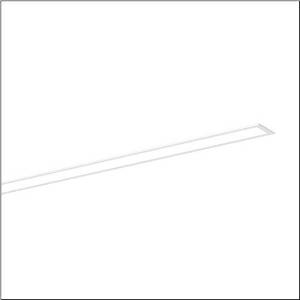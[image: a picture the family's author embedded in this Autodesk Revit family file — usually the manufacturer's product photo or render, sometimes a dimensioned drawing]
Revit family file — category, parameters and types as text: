
# Revit family: silica_r__21_51mx10db32wb_8ee9
name_source: partatom
category: Lighting Fixtures
units: mm (PartAtom-declared; Revit-internal decimal feet)

## family parameters
Cut with Voids When Loaded = No
Host = Face
Light Source = No
Part Type = Normal
Room Calculation Point = No
Round Connector Dimension = Use Diameter
Shared = No

## types (1)
- --- (1 x LED, 3000 lm, 20.2 W, 3000K)
    Apparent Load = 20 VA
    CIE Flux Codes = 48 79 96 100 100
    Color Rendering = 80
    Color Temperature = 3000K
    Default Elevation = 1800 mm
    Description = Silica® 21, office luminaire, primary optical cover: cover, of PMMA, opal, light emission: direct distribution, primary light characteristic: symmetric, installation type: recessed, LED, rated luminous flux: 3.000lm, luminous efficacy: 149lm/W, light colour: 830, colour temperature: 3000K, control gear: DALI 2, with terminal, 3+2-pole, max. 2.5mm², mains connection: 220..240V, AC, 50/60Hz, luminaire housing, of aluminium, traffic white (RAL 9016), length: 1.528mm, width: 79mm, height: 53mm, protection rating (complete): IP20, insulation class (complete): insulation class I (protective earthing), certification: CE, ENEC, VDE, permissible operating ambient temperature: 0..+35°C, standard: EN 50419, packaging unit: 1 piece
    Height = 0 mm  [stored 0 ft]
    Lamp = 1 x LED
    Lamp Light Flux = 3000 lm
    Lamp Power = 20.2 W
    Lamp count = 1
    Length = 1527 mm
    Luminous efficacy = 149 lm/W
    Manufacturer = Siteco
    ModVariant = No
    Model = 51MX10DB32WB
    Mounting Place = Ceiling
    Mounting Type = Recessed
    Number of Poles = 1
    OnlyDefault = Yes
    Power Factor = 1
    Product Name = Silica® 21
    Product group = office luminaire | ceiling recessed
    ProductGroupID = 401
    Protection Class = Protection class I
    Protection Degree = IP 20
    RLX_Detail_Level = 1
    RLX_Emergency_Light_Flux = 0 lm
    RLX_Emergency_Type = 0
    RLX_Emergency_Type_DB = No
    RlxData = <blob elided: 20925 chars, md5=9f4012b8>
    Socket = socket
    Standby Power = 0 W
    System Light Flux = 3000 lm
    System Power = 20 W
    Type Comments = factory setting: luminous flux: 100 % | dim-lin: 254 | 233 mA
    Type Image = l_1335891.jpg
    URL = http://relux.com
    VarID = @adj_117638
    Voltage = 0 V
    Weight = 0.00 kg
    Width = 79 mm

note: [stored X ft] marks values corroborated as IEEE doubles in the binary element streams (Revit-internal decimal feet)

## geometry (parser evidence)
native form markers: Blend x4, Sweep x10
no freeform markers — native parametric forms only
